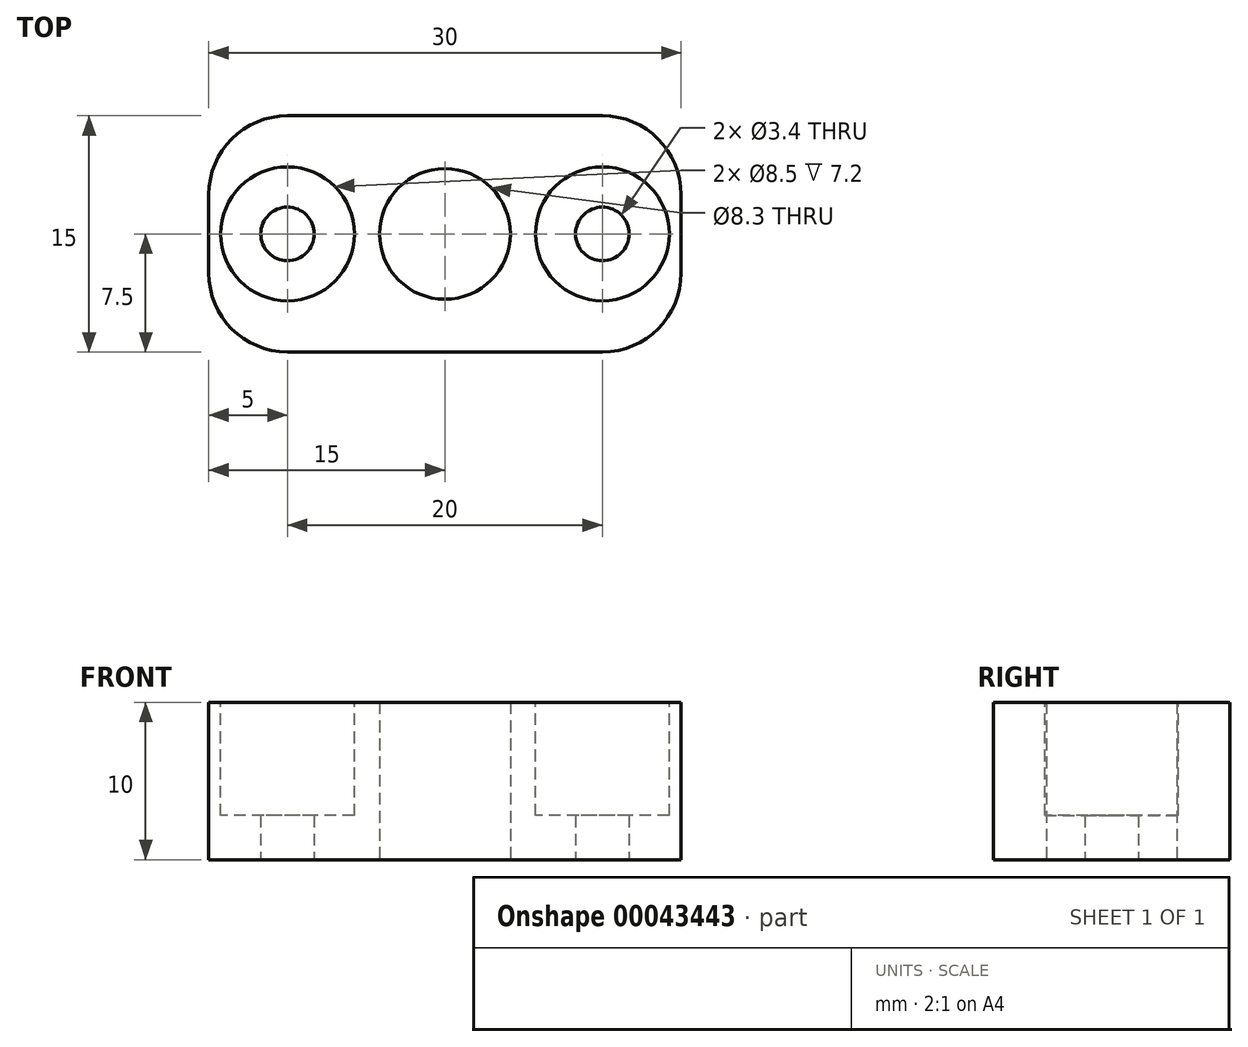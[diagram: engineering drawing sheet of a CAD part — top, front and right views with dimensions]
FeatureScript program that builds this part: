
annotation { "Feature Type Name" : "Feature", "Feature Type Description" : "" }
export const myFeature = defineFeature(function(context is Context, id is Id, definition is map)
    precondition{}
    {
        {
            var Q0;
            Q0=qCreatedBy(makeId("Top.planeOp"),FACE);
            var sketch = newSketch(context, id + "F0", { "sketchPlane" : qUnion([Q0])});
            skLineSegment(sketch, "E0.rect.bottom", {"start": v(10, -7.5) * mm, "end": v(-10, -7.5) * mm});
            skLineSegment(sketch, "E0.rect.top", {"start": v(10, 7.5) * mm, "end": v(-10, 7.5) * mm});
            skLineSegment(sketch, "E0.rect.left", {"start": v(15, -2.5) * mm, "end": v(15, 2.5) * mm});
            skLineSegment(sketch, "E0.rect.right", {"start": v(-15, -2.5) * mm, "end": v(-15, 2.5) * mm});
            skPoint(sketch, "E0.rect.middle", {"position": v(0, 0) * mm});
            skCircle(sketch, "E1", {"center": v(0, 0) * mm, "radius": 4.15 * mm});
            skCircle(sketch, "E2", {"center": v(-10, 0) * mm, "radius": 1.7 * mm});
            skCircle(sketch, "E3", {"center": v(10, 0) * mm, "radius": 1.7 * mm});
            skPoint(sketch, "E4.visualSharp", {"position": v(15, 7.5) * mm});
            skArc(sketch, "E4.filletArc", {"start": v(15, 2.5) * mm, "mid": v(13.54, 6.04) * mm, "end": v(10, 7.5) * mm});
            skPoint(sketch, "E5.visualSharp", {"position": v(15, -7.5) * mm});
            skArc(sketch, "E5.filletArc", {"start": v(10, -7.5) * mm, "mid": v(13.54, -6.04) * mm, "end": v(15, -2.5) * mm});
            skPoint(sketch, "E6.visualSharp", {"position": v(-15, -7.5) * mm});
            skArc(sketch, "E6.filletArc", {"start": v(-15, -2.5) * mm, "mid": v(-13.54, -6.04) * mm, "end": v(-10, -7.5) * mm});
            skPoint(sketch, "E7.visualSharp", {"position": v(-15, 7.5) * mm});
            skArc(sketch, "E7.filletArc", {"start": v(-10, 7.5) * mm, "mid": v(-13.54, 6.04) * mm, "end": v(-15, 2.5) * mm});
            skSolve(sketch);
        }
        {
            var Q0;
            Q0 = qSketchRegion(id + "F0", true);
            extrude(context, id + "F1", {"entities" : qUnion([Q0]), "depth" : 10 * mm});
        }
        {
            var Q0;
            Q0=makeQuery(id+"F1.opExtrude","CAP_FACE",FACE,{"disambiguationData":[OSD([sQuery(id+"F0.wireOp",EDGE,"E0.rect.bottom"),sQuery(id+"F0.wireOp",EDGE,"E0.rect.top"),sQuery(id+"F0.wireOp",EDGE,"E0.rect.left"),sQuery(id+"F0.wireOp",EDGE,"E0.rect.right"),sQuery(id+"F0.wireOp",EDGE,"E1"),sQuery(id+"F0.wireOp",EDGE,"E2"),sQuery(id+"F0.wireOp",EDGE,"E3"),sQuery(id+"F0.wireOp",EDGE,"E4.filletArc"),sQuery(id+"F0.wireOp",EDGE,"E5.filletArc"),sQuery(id+"F0.wireOp",EDGE,"E6.filletArc"),sQuery(id+"F0.wireOp",EDGE,"E7.filletArc")])],"isStart":false});
            var sketch = newSketch(context, id + "F2", { "sketchPlane" : qUnion([Q0])});
            skCircle(sketch, "E8", {"center": v(-10, 0) * mm, "radius": 4.25 * mm});
            skCircle(sketch, "E9", {"center": v(10, 0) * mm, "radius": 4.25 * mm});
            skSolve(sketch);
        }
        {
            var Q0;
            Q0 = qSketchRegion(id + "F2", true);
            extrude(context, id + "F3", {"entities" : qUnion([Q0]), "operationType" : NewBodyOperationType.REMOVE, "oppositeDirection" : true, "depth" : 7.2 * mm});
        }
    });
